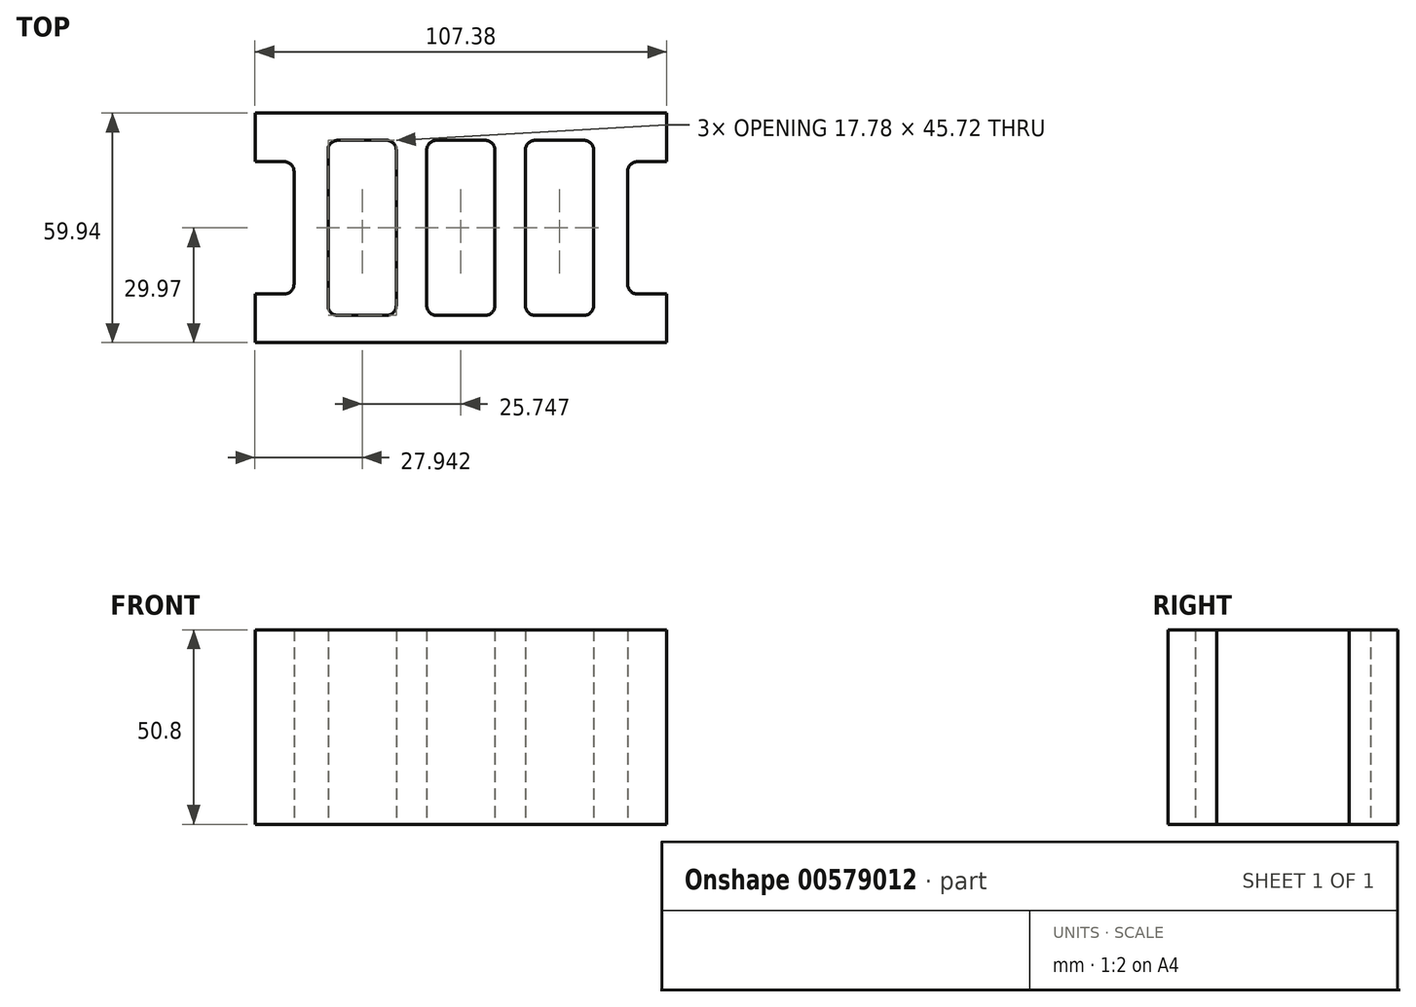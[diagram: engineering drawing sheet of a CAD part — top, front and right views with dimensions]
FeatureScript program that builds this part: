
annotation { "Feature Type Name" : "Feature", "Feature Type Description" : "" }
export const myFeature = defineFeature(function(context is Context, id is Id, definition is map)
    precondition{}
    {
        {
            var Q0;
            Q0=qCreatedBy(makeId("Top.planeOp"),FACE);
            var sketch = newSketch(context, id + "F0", { "sketchPlane" : qUnion([Q0])});
            skLineSegment(sketch, "E0.bottom", {"start": v(-53.69, 29.97) * mm, "end": v(53.69, 29.97) * mm});
            skLineSegment(sketch, "E0.top", {"start": v(-53.69, -29.97) * mm, "end": v(53.69, -29.97) * mm});
            skLineSegment(sketch, "E0.left", {"start": v(-53.69, 29.97) * mm, "end": v(-53.69, -29.97) * mm});
            skLineSegment(sketch, "E0.right", {"start": v(53.69, 29.97) * mm, "end": v(53.69, -29.97) * mm});
            skPoint(sketch, "E0.middle", {"position": v(0, 0) * mm});
            skLineSegment(sketch, "E1", {"start": v(-53.69, 17.27) * mm, "end": v(-46.07, 17.27) * mm});
            skLineSegment(sketch, "E2", {"start": v(-43.53, 14.73) * mm, "end": v(-43.53, -14.73) * mm});
            skLineSegment(sketch, "E3", {"start": v(-46.07, -17.27) * mm, "end": v(-53.69, -17.27) * mm});
            skLineSegment(sketch, "E4", {"start": v(53.69, 17.27) * mm, "end": v(46.07, 17.27) * mm});
            skLineSegment(sketch, "E5", {"start": v(43.53, 14.73) * mm, "end": v(43.53, -14.73) * mm});
            skLineSegment(sketch, "E6", {"start": v(46.07, -17.27) * mm, "end": v(53.69, -17.27) * mm});
            skPoint(sketch, "E7.visualSharp", {"position": v(-43.53, 17.27) * mm});
            skArc(sketch, "E7.filletArc", {"start": v(-43.53, 14.73) * mm, "mid": v(-44.27, 16.53) * mm, "end": v(-46.07, 17.27) * mm});
            skPoint(sketch, "E8.visualSharp", {"position": v(-43.53, -17.27) * mm});
            skArc(sketch, "E8.filletArc", {"start": v(-46.07, -17.27) * mm, "mid": v(-44.27, -16.53) * mm, "end": v(-43.53, -14.73) * mm});
            skPoint(sketch, "E9.visualSharp", {"position": v(43.53, 17.27) * mm});
            skArc(sketch, "E9.filletArc", {"start": v(46.07, 17.27) * mm, "mid": v(44.27, 16.53) * mm, "end": v(43.53, 14.73) * mm});
            skPoint(sketch, "E10.visualSharp", {"position": v(43.53, -17.27) * mm});
            skArc(sketch, "E10.filletArc", {"start": v(43.53, -14.73) * mm, "mid": v(44.27, -16.53) * mm, "end": v(46.07, -17.27) * mm});
            skLineSegment(sketch, "E11", {"start": v(-43.53, 0) * mm, "end": v(0, 0) * mm});
            skLineSegment(sketch, "E12", {"start": v(43.53, 0) * mm, "end": v(0, 0) * mm});
            skPoint(sketch, "E13", {"position": v(-25.75, 0) * mm});
            skPoint(sketch, "E14", {"position": v(-3.39, 0) * mm});
            skPoint(sketch, "E15", {"position": v(25.75, 0) * mm});
            skLineSegment(sketch, "E16.bottom", {"start": v(-32.1, 22.86) * mm, "end": v(-19.4, 22.86) * mm});
            skLineSegment(sketch, "E16.top", {"start": v(-32.1, -22.86) * mm, "end": v(-19.4, -22.86) * mm});
            skLineSegment(sketch, "E16.left", {"start": v(-34.64, 20.32) * mm, "end": v(-34.64, -20.32) * mm});
            skLineSegment(sketch, "E16.right", {"start": v(-16.86, 20.32) * mm, "end": v(-16.86, -20.32) * mm});
            skLineSegment(sketch, "E17.bottom", {"start": v(-6.35, 22.86) * mm, "end": v(6.35, 22.86) * mm});
            skLineSegment(sketch, "E17.top", {"start": v(-6.35, -22.86) * mm, "end": v(6.35, -22.86) * mm});
            skLineSegment(sketch, "E17.left", {"start": v(-8.89, 20.32) * mm, "end": v(-8.9, -20.32) * mm});
            skLineSegment(sketch, "E17.right", {"start": v(8.9, 20.32) * mm, "end": v(8.89, -20.32) * mm});
            skLineSegment(sketch, "E18.bottom", {"start": v(19.4, 22.86) * mm, "end": v(32.1, 22.86) * mm});
            skLineSegment(sketch, "E18.top", {"start": v(19.4, -22.86) * mm, "end": v(32.1, -22.86) * mm});
            skLineSegment(sketch, "E18.left", {"start": v(16.86, 20.32) * mm, "end": v(16.86, -20.32) * mm});
            skLineSegment(sketch, "E18.right", {"start": v(34.64, 20.32) * mm, "end": v(34.64, -20.32) * mm});
            skPoint(sketch, "E19.visualSharp", {"position": v(-8.89, 22.86) * mm});
            skArc(sketch, "E19.filletArc", {"start": v(-6.35, 22.86) * mm, "mid": v(-8.15, 22.12) * mm, "end": v(-8.89, 20.32) * mm});
            skPoint(sketch, "E20.visualSharp", {"position": v(8.9, 22.86) * mm});
            skArc(sketch, "E20.filletArc", {"start": v(8.9, 20.32) * mm, "mid": v(8.15, 22.12) * mm, "end": v(6.35, 22.86) * mm});
            skPoint(sketch, "E21.visualSharp", {"position": v(8.89, -22.86) * mm});
            skArc(sketch, "E21.filletArc", {"start": v(6.35, -22.86) * mm, "mid": v(8.15, -22.12) * mm, "end": v(8.89, -20.32) * mm});
            skPoint(sketch, "E22.visualSharp", {"position": v(-8.9, -22.86) * mm});
            skArc(sketch, "E22.filletArc", {"start": v(-8.9, -20.32) * mm, "mid": v(-8.15, -22.12) * mm, "end": v(-6.35, -22.86) * mm});
            skPoint(sketch, "E23.visualSharp", {"position": v(-16.86, -22.86) * mm});
            skArc(sketch, "E23.filletArc", {"start": v(-19.4, -22.86) * mm, "mid": v(-17.6, -22.12) * mm, "end": v(-16.86, -20.32) * mm});
            skPoint(sketch, "E24.visualSharp", {"position": v(-16.86, 22.86) * mm});
            skArc(sketch, "E24.filletArc", {"start": v(-16.86, 20.32) * mm, "mid": v(-17.6, 22.12) * mm, "end": v(-19.4, 22.86) * mm});
            skPoint(sketch, "E25.visualSharp", {"position": v(-34.64, 22.86) * mm});
            skArc(sketch, "E25.filletArc", {"start": v(-32.1, 22.86) * mm, "mid": v(-33.9, 22.12) * mm, "end": v(-34.64, 20.32) * mm});
            skPoint(sketch, "E26.visualSharp", {"position": v(-34.64, -22.86) * mm});
            skArc(sketch, "E26.filletArc", {"start": v(-34.64, -20.32) * mm, "mid": v(-33.9, -22.12) * mm, "end": v(-32.1, -22.86) * mm});
            skPoint(sketch, "E27.visualSharp", {"position": v(34.64, 22.86) * mm});
            skArc(sketch, "E27.filletArc", {"start": v(34.64, 20.32) * mm, "mid": v(33.9, 22.12) * mm, "end": v(32.1, 22.86) * mm});
            skPoint(sketch, "E28.visualSharp", {"position": v(16.86, 22.86) * mm});
            skArc(sketch, "E28.filletArc", {"start": v(19.4, 22.86) * mm, "mid": v(17.6, 22.12) * mm, "end": v(16.86, 20.32) * mm});
            skPoint(sketch, "E29.visualSharp", {"position": v(16.86, -22.86) * mm});
            skArc(sketch, "E29.filletArc", {"start": v(16.86, -20.32) * mm, "mid": v(17.6, -22.12) * mm, "end": v(19.4, -22.86) * mm});
            skPoint(sketch, "E30.visualSharp", {"position": v(34.64, -22.86) * mm});
            skArc(sketch, "E30.filletArc", {"start": v(32.1, -22.86) * mm, "mid": v(33.9, -22.12) * mm, "end": v(34.64, -20.32) * mm});
            skSolve(sketch);
        }
        {
            var Q0;
            {var subQ11=sQuery(id+"F0.wireOp",EDGE,"E0.bottom");Q0=makeQuery(id+"F0.imprint","IMPRINT",FACE,{"disambiguationData":[TD([[makeQuery(id+"F0.imprint","IMPRINT",EDGE,{"derivedFrom":subQ11}),-1.0]])]});}
            var Q1;
            {var subQ17=sQuery(id+"F0.wireOp",EDGE,"E0.top");Q1=makeQuery(id+"F0.imprint","IMPRINT",FACE,{"disambiguationData":[TD([[makeQuery(id+"F0.imprint","IMPRINT",EDGE,{"derivedFrom":subQ17}),1.0]])]});}
            extrude(context, id + "F1", {"entities" : qUnion([Q0, Q1]), "depth" : 50.8 * mm, "offsetDistance" : 25.4 * mm});
        }
    });
